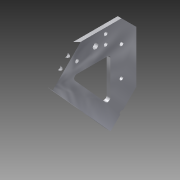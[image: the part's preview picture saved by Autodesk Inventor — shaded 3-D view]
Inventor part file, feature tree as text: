
AUTODESK INVENTOR PART (.ipt)
format: ipt  version: 2015 SP1 (Build 190203100, 203)  size: 177,152 bytes
history: native  units: in
note: dims shown in document units (in); Inventor stores cm internally (conversion verified against a paired STEP export)
features: sketch x6, extrude x4, hole x2, projected_geometry x1
ambient origin geometry x8: Origin, YZ Plane, XZ Plane, XY Plane, X Axis, Y Axis, Z Axis, Center Point
bodies: Solid1 (feature_tree)
feature tree (13):
  extrude  "Extrusion1"  Depth=6.0in
  hole  "Hole1"  [1 undecoded]
  extrude  "Extrusion2"  Depth=1.0in
  hole  "Hole2"  [1 undecoded]
  extrude  "Extrusion3"  Depth=1.0in
  extrude  "Extrusion4"  Depth=1.0in
  sketch  "Sketch1"  dims[d0=6.5in d1=6.0in]
  sketch  "Sketch2"  dims[d2=1.5in d3=1.5in]
  sketch  "Sketch3"  dims[d4=0.25in d5=0.0in d6=1.0in]
  sketch  "Sketch4"  dims[d7=1.0in d8=1.0in]
  sketch  "Sketch5"  dims[d9=1.0in d10=2.0in]
  sketch  "Sketch6"  dims[d11=2.0in d12=0.25in d13=0.75in d14=0.375in d15=0.25in d16=0.5635in d17=1.0in d18=0.8108in d19=1.0in d20=45.0deg d21=0.25in d22=0.0in d23=0.5in d24=0.5in d25=1.0in d26=1.0in d27=0.5in d28=1.5in d29=2.0in d30=1.0in d31=0.25in d32=0.75in d33=0.375in d34=0.25in d35=0.5635in d36=1.0in d37=0.8108in d38=2.0625in d39=2.0625in d40=2.75in d41=0.75in d42=0.375in d43=1.0in d44=0.375in d45=0.25in d46=0.25in d47=0.25in d48=0.0in d49=0.25in d50=0.25in d52=1.0in d53=0.1875in d54=1.0in d55=0.0in]
  projected_geometry  "Projected Loop1"
note: 2 required parameter values undecoded (feature->parameter linkage not recoverable at this tier; creation-order binding heuristic only, values carry confidence <= 0.55)
